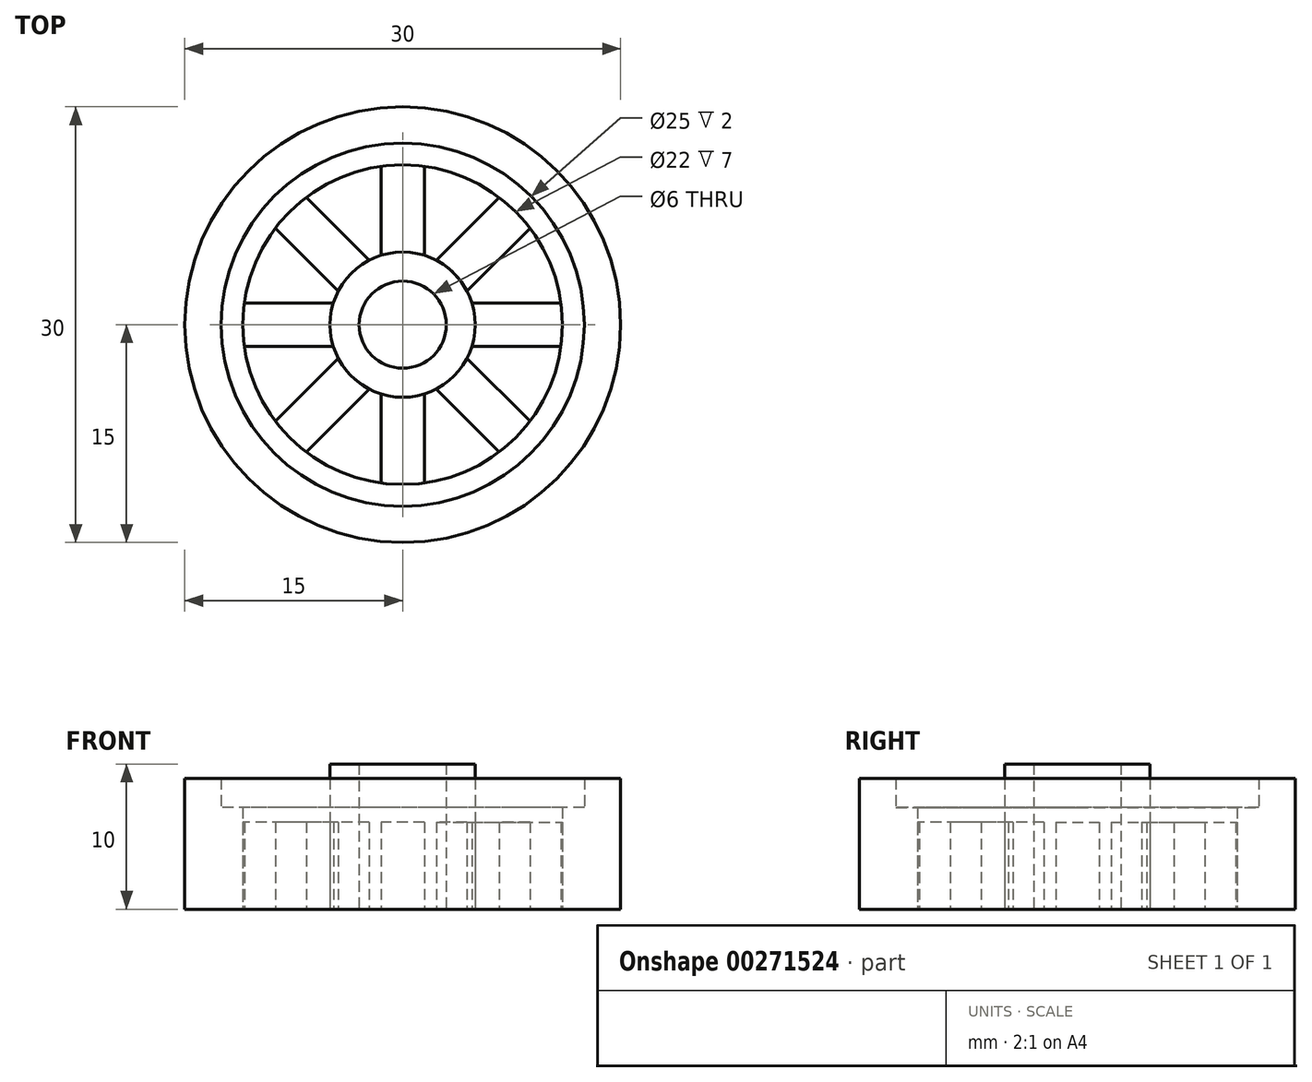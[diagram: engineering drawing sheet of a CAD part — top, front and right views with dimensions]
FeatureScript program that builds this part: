
annotation { "Feature Type Name" : "Feature", "Feature Type Description" : "" }
export const myFeature = defineFeature(function(context is Context, id is Id, definition is map)
    precondition{}
    {
        {
            var Q0;
            Q0=qCreatedBy(makeId("Top.planeOp"),FACE);
            var sketch = newSketch(context, id + "F0", { "sketchPlane" : qUnion([Q0])});
            skCircle(sketch, "E0", {"center": v(0, 0) * mm, "radius": 12.5 * mm});
            skCircle(sketch, "E1", {"center": v(0, 0) * mm, "radius": 11 * mm});
            skCircle(sketch, "E2", {"center": v(0, 0) * mm, "radius": 3 * mm});
            skCircle(sketch, "E3", {"center": v(0, 0) * mm, "radius": 5 * mm});
            skCircle(sketch, "E4", {"center": v(0, 0) * mm, "radius": 15 * mm});
            skPoint(sketch, "E5.middle", {"position": v(0, 7.86) * mm});
            skPoint(sketch, "E6.orphan", {"position": v(-2, 14.2) * mm});
            skPoint(sketch, "E7.orphan", {"position": v(2, 14.2) * mm});
            skLineSegment(sketch, "E8.trimOffspring", {"start": v(-1.5, 4.77) * mm, "end": v(-1.5, 10.9) * mm});
            skLineSegment(sketch, "E9.trimOffspring", {"start": v(1.5, 4.77) * mm, "end": v(1.5, 10.9) * mm});
            skPoint(sketch, "E5.right.start.orphan", {"position": v(-2, 1.53) * mm});
            skPoint(sketch, "E5.left.start.orphan", {"position": v(2, 1.53) * mm});
            skSolve(sketch);
        }
        {
            var Q0;
            Q0=makeQuery(id+"F0.imprint","IMPRINT",FACE,{"disambiguationData":[TD([[makeQuery(id+"F0.imprint","IMPRINT",EDGE,{"derivedFrom":sQuery(id+"F0.wireOp",EDGE,"E2")}),-1.0]])]});
            extrude(context, id + "F1", {"entities" : qUnion([Q0]), "depth" : 10 * mm});
        }
        {
            var Q0;
            Q0=makeQuery(id+"F0.imprint","IMPRINT",FACE,{"disambiguationData":[TD([[makeQuery(id+"F0.imprint","IMPRINT",EDGE,{"derivedFrom":sQuery(id+"F0.wireOp",EDGE,"E0")}),-1.0]])]});
            extrude(context, id + "F2", {"entities" : qUnion([Q0]), "depth" : 9 * mm});
        }
        {
            var Q0;
            Q0=makeQuery(id+"F0.imprint","IMPRINT",FACE,{"disambiguationData":[TD([[makeQuery(id+"F0.imprint","IMPRINT",EDGE,{"derivedFrom":sQuery(id+"F0.wireOp",EDGE,"E0")}),1.0]])]});
            extrude(context, id + "F3", {"entities" : qUnion([Q0]), "operationType" : NewBodyOperationType.ADD, "depth" : 7 * mm});
        }
        {
            var Q0;
            {var subQ0=sQuery(id+"F0.wireOp",EDGE,"E8.trimOffspring");Q0=makeQuery(id+"F0.imprint","IMPRINT",FACE,{"disambiguationData":[TD([[makeQuery(id+"F0.imprint","IMPRINT",EDGE,{"derivedFrom":subQ0}),-1.0]])]});}
            extrude(context, id + "F4", {"entities" : qUnion([Q0]), "depth" : 6 * mm});
        }
        {
            var Q0;
            Q0=makeQuery(id+"F4.opExtrude","SWEPT_BODY",BODY,{"disambiguationData":[OSD([sQuery(id+"F0.wireOp",EDGE,"E1"),sQuery(id+"F0.wireOp",EDGE,"E3"),sQuery(id+"F0.wireOp",EDGE,"E8.trimOffspring"),sQuery(id+"F0.wireOp",EDGE,"E9.trimOffspring")])]});
            var Q1;
            Q1=makeQuery(id+"F1.opExtrude","SWEPT_FACE",FACE,{"disambiguationData":[OSD([sQuery(id+"F0.wireOp",EDGE,"E3")])]});
            transform(context, id + "F5", {"entities" : qUnion([Q0]), "transformType" : TransformType.ROTATION, "transformAxis" : qUnion([Q1]), "angle" : 45 * degree, "makeCopy" : true});
        }
        {
            var Q0;
            Q0=makeQuery(id+"F5.opPattern","COPY",BODY,{"derivedFrom":makeQuery(id+"F4.opExtrude","SWEPT_BODY",BODY,{"disambiguationData":[OSD([sQuery(id+"F0.wireOp",EDGE,"E1"),sQuery(id+"F0.wireOp",EDGE,"E3"),sQuery(id+"F0.wireOp",EDGE,"E8.trimOffspring"),sQuery(id+"F0.wireOp",EDGE,"E9.trimOffspring")])]}),"instanceName":"1"});
            var Q1;
            Q1=makeQuery(id+"F1.opExtrude","SWEPT_FACE",FACE,{"disambiguationData":[OSD([sQuery(id+"F0.wireOp",EDGE,"E3")])]});
            transform(context, id + "F6", {"entities" : qUnion([Q0]), "transformType" : TransformType.ROTATION, "transformAxis" : qUnion([Q1]), "angle" : 45 * degree, "makeCopy" : true});
        }
        {
            var Q0;
            Q0=makeQuery(id+"F6.opPattern","COPY",BODY,{"derivedFrom":makeQuery(id+"F5.opPattern","COPY",BODY,{"derivedFrom":makeQuery(id+"F4.opExtrude","SWEPT_BODY",BODY,{"disambiguationData":[OSD([sQuery(id+"F0.wireOp",EDGE,"E1"),sQuery(id+"F0.wireOp",EDGE,"E3"),sQuery(id+"F0.wireOp",EDGE,"E8.trimOffspring"),sQuery(id+"F0.wireOp",EDGE,"E9.trimOffspring")])]}),"instanceName":"1"}),"instanceName":"1"});
            var Q1;
            Q1=makeQuery(id+"F1.opExtrude","SWEPT_FACE",FACE,{"disambiguationData":[OSD([sQuery(id+"F0.wireOp",EDGE,"E3")])]});
            transform(context, id + "F7", {"entities" : qUnion([Q0]), "transformType" : TransformType.ROTATION, "transformAxis" : qUnion([Q1]), "angle" : 45 * degree, "makeCopy" : true});
        }
        {
            var Q0;
            Q0=makeQuery(id+"F7.opPattern","COPY",BODY,{"derivedFrom":makeQuery(id+"F6.opPattern","COPY",BODY,{"derivedFrom":makeQuery(id+"F5.opPattern","COPY",BODY,{"derivedFrom":makeQuery(id+"F4.opExtrude","SWEPT_BODY",BODY,{"disambiguationData":[OSD([sQuery(id+"F0.wireOp",EDGE,"E1"),sQuery(id+"F0.wireOp",EDGE,"E3"),sQuery(id+"F0.wireOp",EDGE,"E8.trimOffspring"),sQuery(id+"F0.wireOp",EDGE,"E9.trimOffspring")])]}),"instanceName":"1"}),"instanceName":"1"}),"instanceName":"1"});
            var Q1;
            Q1=makeQuery(id+"F1.opExtrude","SWEPT_FACE",FACE,{"disambiguationData":[OSD([sQuery(id+"F0.wireOp",EDGE,"E3")])]});
            transform(context, id + "F8", {"entities" : qUnion([Q0]), "transformType" : TransformType.ROTATION, "transformAxis" : qUnion([Q1]), "angle" : 45 * degree, "makeCopy" : true});
        }
        {
            var Q0;
            Q0=makeQuery(id+"F8.opPattern","COPY",BODY,{"derivedFrom":makeQuery(id+"F7.opPattern","COPY",BODY,{"derivedFrom":makeQuery(id+"F6.opPattern","COPY",BODY,{"derivedFrom":makeQuery(id+"F5.opPattern","COPY",BODY,{"derivedFrom":makeQuery(id+"F4.opExtrude","SWEPT_BODY",BODY,{"disambiguationData":[OSD([sQuery(id+"F0.wireOp",EDGE,"E1"),sQuery(id+"F0.wireOp",EDGE,"E3"),sQuery(id+"F0.wireOp",EDGE,"E8.trimOffspring"),sQuery(id+"F0.wireOp",EDGE,"E9.trimOffspring")])]}),"instanceName":"1"}),"instanceName":"1"}),"instanceName":"1"}),"instanceName":"1"});
            var Q1;
            Q1=makeQuery(id+"F1.opExtrude","CAP_EDGE",EDGE,{"disambiguationData":[OSD([sQuery(id+"F0.wireOp",EDGE,"E3")])],"isStart":true});
            transform(context, id + "F9", {"entities" : qUnion([Q0]), "transformType" : TransformType.ROTATION, "transformAxis" : qUnion([Q1]), "angle" : 45 * degree, "oppositeDirection" : true, "makeCopy" : true});
        }
        {
            var Q0;
            Q0=makeQuery(id+"F9.opPattern","COPY",BODY,{"derivedFrom":makeQuery(id+"F8.opPattern","COPY",BODY,{"derivedFrom":makeQuery(id+"F7.opPattern","COPY",BODY,{"derivedFrom":makeQuery(id+"F6.opPattern","COPY",BODY,{"derivedFrom":makeQuery(id+"F5.opPattern","COPY",BODY,{"derivedFrom":makeQuery(id+"F4.opExtrude","SWEPT_BODY",BODY,{"disambiguationData":[OSD([sQuery(id+"F0.wireOp",EDGE,"E1"),sQuery(id+"F0.wireOp",EDGE,"E3"),sQuery(id+"F0.wireOp",EDGE,"E8.trimOffspring"),sQuery(id+"F0.wireOp",EDGE,"E9.trimOffspring")])]}),"instanceName":"1"}),"instanceName":"1"}),"instanceName":"1"}),"instanceName":"1"}),"instanceName":"1"});
            var Q1;
            Q1=makeQuery(id+"F1.opExtrude","CAP_EDGE",EDGE,{"disambiguationData":[OSD([sQuery(id+"F0.wireOp",EDGE,"E3")])],"isStart":true});
            transform(context, id + "F10", {"entities" : qUnion([Q0]), "transformType" : TransformType.ROTATION, "transformAxis" : qUnion([Q1]), "angle" : 45 * degree, "oppositeDirection" : true, "makeCopy" : true});
        }
        {
            var Q0;
            Q0=makeQuery(id+"F10.opPattern","COPY",BODY,{"derivedFrom":makeQuery(id+"F9.opPattern","COPY",BODY,{"derivedFrom":makeQuery(id+"F8.opPattern","COPY",BODY,{"derivedFrom":makeQuery(id+"F7.opPattern","COPY",BODY,{"derivedFrom":makeQuery(id+"F6.opPattern","COPY",BODY,{"derivedFrom":makeQuery(id+"F5.opPattern","COPY",BODY,{"derivedFrom":makeQuery(id+"F4.opExtrude","SWEPT_BODY",BODY,{"disambiguationData":[OSD([sQuery(id+"F0.wireOp",EDGE,"E1"),sQuery(id+"F0.wireOp",EDGE,"E3"),sQuery(id+"F0.wireOp",EDGE,"E8.trimOffspring"),sQuery(id+"F0.wireOp",EDGE,"E9.trimOffspring")])]}),"instanceName":"1"}),"instanceName":"1"}),"instanceName":"1"}),"instanceName":"1"}),"instanceName":"1"}),"instanceName":"1"});
            var Q1;
            Q1=makeQuery(id+"F1.opExtrude","SWEPT_FACE",FACE,{"disambiguationData":[OSD([sQuery(id+"F0.wireOp",EDGE,"E3")])]});
            transform(context, id + "F11", {"entities" : qUnion([Q0]), "transformType" : TransformType.ROTATION, "transformAxis" : qUnion([Q1]), "angle" : 45 * degree, "makeCopy" : true});
        }
    });
